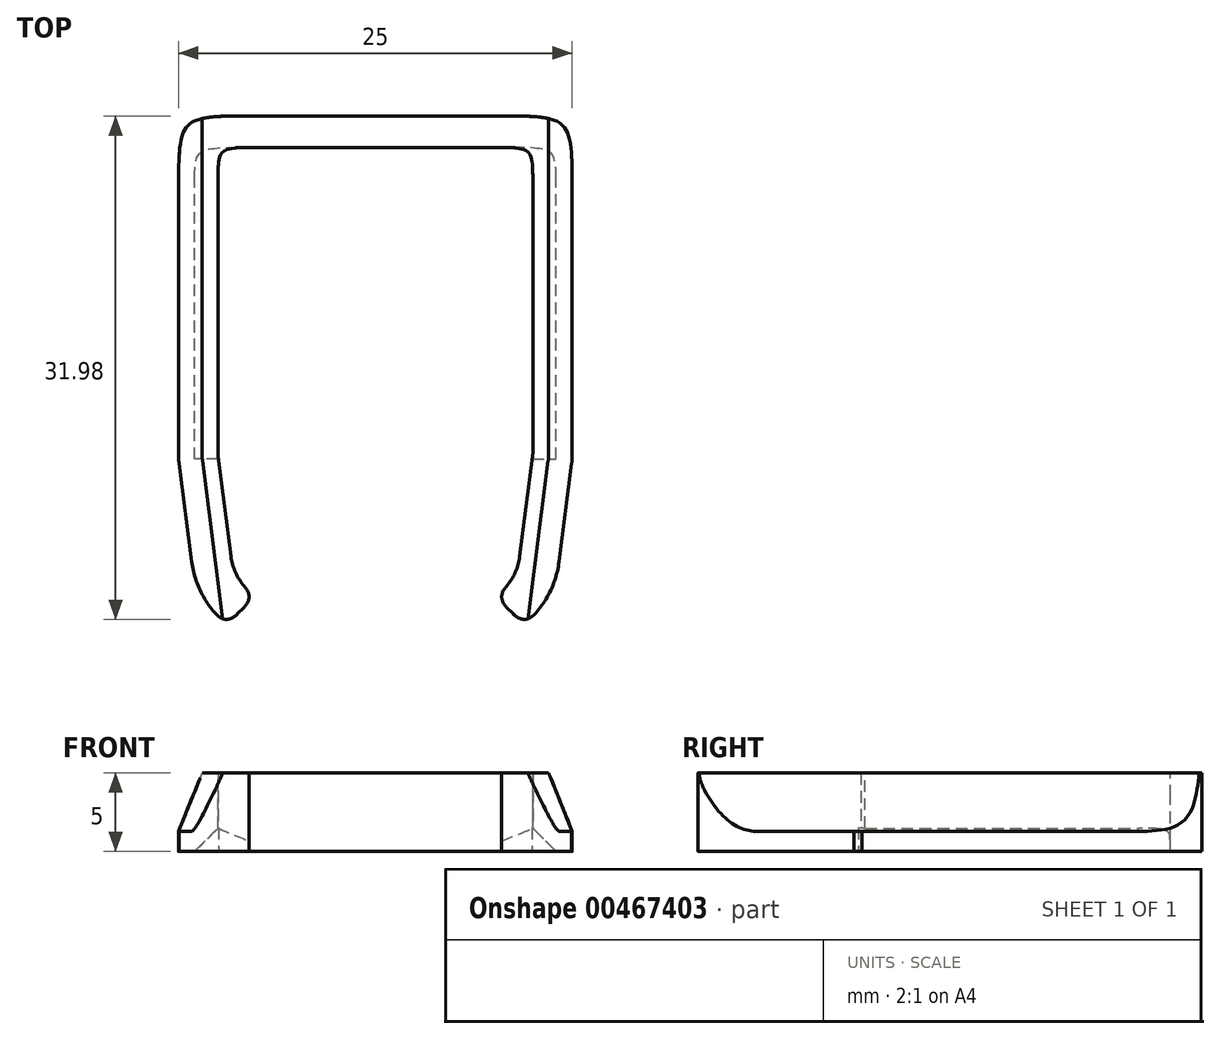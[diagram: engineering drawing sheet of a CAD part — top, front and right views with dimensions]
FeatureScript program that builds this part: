
annotation { "Feature Type Name" : "Feature", "Feature Type Description" : "" }
export const myFeature = defineFeature(function(context is Context, id is Id, definition is map)
    precondition{}
    {
        {
            var Q0;
            Q0=qCreatedBy(makeId("Top.planeOp"),FACE);
            var sketch = newSketch(context, id + "F0", { "sketchPlane" : qUnion([Q0])});
            skLineSegment(sketch, "E0", {"start": v(0, 0) * mm, "end": v(7.15, 0) * mm});
            skLineSegment(sketch, "E1", {"start": v(7.15, 0) * mm, "end": v(7.15, -3) * mm});
            skArc(sketch, "E2", {"start": v(8.15, -9.67) * mm, "mid": v(9.96, -5.99) * mm, "end": v(7.15, -3) * mm});
            skLineSegment(sketch, "E3", {"start": v(7.15, -3) * mm, "end": v(0, -3) * mm, "construction": true});
            skLineSegment(sketch, "E4", {"start": v(10, -6.52) * mm, "end": v(10, 0) * mm, "construction": true});
            skLineSegment(sketch, "E5", {"start": v(10, 0) * mm, "end": v(7.15, 0) * mm, "construction": true});
            skSolve(sketch);
        }
        {
            var Q0;
            Q0=qCreatedBy(makeId("Top.planeOp"),FACE);
            var sketch = newSketch(context, id + "F1", { "sketchPlane" : qUnion([Q0])});
            skLineSegment(sketch, "E6", {"start": v(0, 19) * mm, "end": v(0, 21) * mm});
            skLineSegment(sketch, "E7", {"start": v(0, 21) * mm, "end": v(12.5, 21) * mm});
            skLineSegment(sketch, "E8", {"start": v(9.42, -11.3) * mm, "end": v(7.62, -9.5) * mm});
            skLineSegment(sketch, "E9", {"start": v(0, 19) * mm, "end": v(10, 19) * mm});
            skLineSegment(sketch, "E10", {"start": v(10, -0.5) * mm, "end": v(9.17, -6.98) * mm});
            skArc(sketch, "E11", {"start": v(7.62, -9.5) * mm, "mid": v(8.67, -8.4) * mm, "end": v(9.17, -6.98) * mm});
            skLineSegment(sketch, "E12", {"start": v(12.5, -0.82) * mm, "end": v(11.67, -7.3) * mm});
            skArc(sketch, "E13", {"start": v(9.42, -11.3) * mm, "mid": v(10.94, -9.52) * mm, "end": v(11.67, -7.3) * mm});
            skLineSegment(sketch, "E14", {"start": v(12.5, 21) * mm, "end": v(12.5, -0.82) * mm});
            skLineSegment(sketch, "E15", {"start": v(10, 19) * mm, "end": v(10, -0.5) * mm});
            skLineSegment(sketch, "E16", {"start": v(10, 19) * mm, "end": v(12.5, 19) * mm, "construction": true});
            skLineSegment(sketch, "E17", {"start": v(10, -0.5) * mm, "end": v(12.5, -0.82) * mm, "construction": true});
            skSolve(sketch);
        }
        {
            var Q0;
            Q0=qSketchRegion(id+"F1",true);
            extrude(context, id + "F2", {"entities" : qUnion([Q0]), "depth" : 5 * mm});
        }
        {
            var Q0;
            Q0=makeQuery(id+"F2.opExtrude","SWEPT_EDGE",EDGE,{"disambiguationData":[OSD([sQuery(id+"F1.wireOp",EDGE,"E9"),sQuery(id+"F1.wireOp",EDGE,"E15")])]});
            var Q1;
            Q1=makeQuery(id+"F2.opExtrude","SWEPT_EDGE",EDGE,{"disambiguationData":[OSD([sQuery(id+"F1.wireOp",EDGE,"E10"),sQuery(id+"F1.wireOp",EDGE,"E15")])]});
            fillet(context, id + "F3", {"entities" : qUnion([Q0, Q1]), "radius" : 2 * mm, "tangentPropagation" : true, "rho" : .7, "crossSection" : FilletCrossSection.CONIC, "allowEdgeOverflow" : false});
        }
        {
            var Q0;
            Q0=makeQuery(id+"F2.opExtrude","SWEPT_EDGE",EDGE,{"disambiguationData":[OSD([sQuery(id+"F1.wireOp",EDGE,"E7"),sQuery(id+"F1.wireOp",EDGE,"E14")])]});
            var Q1;
            Q1=makeQuery(id+"F2.opExtrude","SWEPT_EDGE",EDGE,{"disambiguationData":[OSD([sQuery(id+"F1.wireOp",EDGE,"E12"),sQuery(id+"F1.wireOp",EDGE,"E14")])]});
            fillet(context, id + "F4", {"entities" : qUnion([Q0, Q1]), "radius" : 4 * mm, "tangentPropagation" : true, "rho" : .7, "crossSection" : FilletCrossSection.CONIC, "allowEdgeOverflow" : false});
        }
        {
            var Q0;
            Q0=makeQuery(id+"F2.opExtrude","SWEPT_FACE",FACE,{"disambiguationData":[OSD([sQuery(id+"F1.wireOp",EDGE,"E9")])]});
            var sketch = newSketch(context, id + "F5", { "sketchPlane" : qUnion([Q0])});
            skLineSegment(sketch, "E18.bottom", {"start": v(0, 2.5) * mm, "end": v(3, 2.5) * mm});
            skLineSegment(sketch, "E18.top", {"start": v(0, 0) * mm, "end": v(3, 0) * mm});
            skLineSegment(sketch, "E18.left", {"start": v(0, 2.5) * mm, "end": v(0, 0) * mm});
            skLineSegment(sketch, "E18.right", {"start": v(3, 2.5) * mm, "end": v(3, 0) * mm});
            skSolve(sketch);
        }
        {
            var Q0;
            Q0=makeQuery(id+"F13.opPattern","COPY",EDGE,{"derivedFrom":makeQuery(id+"F2.opExtrude","CAP_EDGE",EDGE,{"disambiguationData":[OSD([sQuery(id+"F1.wireOp",EDGE,"E12")])],"isStart":true}),"instanceName":"1"});
            var Q1;
            Q1=makeQuery(id+"F2.opExtrude","CAP_EDGE",EDGE,{"disambiguationData":[OSD([sQuery(id+"F1.wireOp",EDGE,"E12")])],"isStart":false});
            var Q2;
            Q2=makeQuery(id+"F2.opExtrude","CAP_EDGE",EDGE,{"disambiguationData":[OSD([sQuery(id+"F1.wireOp",EDGE,"E14")])],"isStart":false});
            chamfer(context, id + "F6", {"entities" : qUnion([Q0, Q1, Q2]), "chamferType" : ChamferType.OFFSET_ANGLE, "width" : 1.5 * mm, "oppositeDirection" : true, "angle" : 68 * degree});
        }
        {
            var Q0;
            {var subQ3=sQuery(id+"F5.wireOp",EDGE,"E18.bottom");Q0=makeQuery(id+"F5.imprint","IMPRINT",FACE,{"disambiguationData":[TD([[makeQuery(id+"F5.imprint","IMPRINT",EDGE,{"derivedFrom":subQ3}),1.0]])]});}
            var sketch = newSketch(context, id + "F7", { "sketchPlane" : qUnion([Q0])});
            skLineSegment(sketch, "E19", {"start": v(8, 3.48) * mm, "end": v(8, 0) * mm});
            skLineSegment(sketch, "E20", {"start": v(8, 0) * mm, "end": v(11.48, 0) * mm});
            skLineSegment(sketch, "E21", {"start": v(11.48, 0) * mm, "end": v(8, 3.48) * mm});
            skPoint(sketch, "E22", {"position": v(9.98, 0) * mm});
            skSolve(sketch);
        }
        {
            var Q0;
            Q0=qSketchRegion(id+"F7",true);
            extrude(context, id + "F8", {"entities" : qUnion([Q0]), "operationType" : NewBodyOperationType.REMOVE, "depth" : 19.8 * mm});
        }
        {
            var Q0;
            Q0=qCreatedBy(makeId("Front.planeOp"),FACE);
            cPlane(context, id + "F9", {"entities" : qUnion([Q0]), "cplaneType" : CPlaneType.OFFSET, "offset" : 0 * mm, "oppositeDirection" : true, "width" : 150 * mm, "height" : 150 * mm});
        }
        {
            var Q0;
            Q0=qCreatedBy(id+"F9.planeOp",FACE);
            var sketch = newSketch(context, id + "F10", { "sketchPlane" : qUnion([Q0])});
            skLineSegment(sketch, "E23", {"start": v(16.37, 0) * mm, "end": v(14.33, 5) * mm});
            skLineSegment(sketch, "E24", {"start": v(14.33, 5) * mm, "end": v(11.1, 5) * mm});
            skLineSegment(sketch, "E25", {"start": v(16.37, 0) * mm, "end": v(12.6, 0) * mm});
            skLineSegment(sketch, "E26", {"start": v(12.6, 0) * mm, "end": v(11.1, 5) * mm});
            skLineSegment(sketch, "E27", {"start": v(12.6, 1.29) * mm, "end": v(11.1, 5) * mm, "construction": true});
            skSolve(sketch);
        }
        {
            var Q0;
            Q0=makeQuery(id+"F2.opExtrude","SWEPT_EDGE",EDGE,{"disambiguationData":[OSD([sQuery(id+"F1.wireOp",EDGE,"E8"),sQuery(id+"F1.wireOp",EDGE,"E11")])]});
            var Q1;
            Q1=makeQuery(id+"F2.opExtrude","SWEPT_EDGE",EDGE,{"disambiguationData":[OSD([sQuery(id+"F1.wireOp",EDGE,"E8"),sQuery(id+"F1.wireOp",EDGE,"E13")])]});
            var Q2;
            Q2=makeQuery(id+"FeDOwkYFawgQy55_1.opExtrude","CAP_EDGE",EDGE,{"disambiguationData":[OSD([sQuery(id+"F10.wireOp",EDGE,"E23")])],"isStart":true});
            var Q3;
            Q3=makeQuery(id+"FeDOwkYFawgQy55_1.opExtrude","CAP_EDGE",EDGE,{"disambiguationData":[OSD([sQuery(id+"F10.wireOp",EDGE,"E23")])],"isStart":false});
            var Q4;
            Q4=makeQuery(id+"FeDOwkYFawgQy55_1.boolean.opBoolean","INTERSECT",EDGE,{"derivedFrom":[makeQuery(id+"F6.opChamfer","BLEND_FACE",FACE,{"disambiguationData":[OSD([sQuery(id+"F1.wireOp",EDGE,"E12")])]}),makeQuery(id+"FeDOwkYFawgQy55_1.opExtrude","CAP_FACE",FACE,{"disambiguationData":[OSD([sQuery(id+"F10.wireOp",EDGE,"E23"),sQuery(id+"F10.wireOp",EDGE,"E24"),sQuery(id+"F10.wireOp",EDGE,"E25"),sQuery(id+"F10.wireOp",EDGE,"E26")])],"isStart":true})]});
            var Q5;
            Q5=makeQuery(id+"FeDOwkYFawgQy55_1.boolean.opBoolean","INTERSECT",EDGE,{"derivedFrom":[makeQuery(id+"F6.opChamfer","BLEND_FACE",FACE,{"disambiguationData":[OSD([sQuery(id+"F1.wireOp",EDGE,"E12")])]}),makeQuery(id+"FeDOwkYFawgQy55_1.opExtrude","CAP_FACE",FACE,{"disambiguationData":[OSD([sQuery(id+"F10.wireOp",EDGE,"E23"),sQuery(id+"F10.wireOp",EDGE,"E24"),sQuery(id+"F10.wireOp",EDGE,"E25"),sQuery(id+"F10.wireOp",EDGE,"E26")])],"isStart":false})]});
            var Q6;
            Q6=makeQuery(id+"FeDOwkYFawgQy55_1.boolean.opBoolean","INTERSECT",EDGE,{"derivedFrom":[makeQuery(id+"F2.opExtrude","SWEPT_FACE",FACE,{"disambiguationData":[OSD([sQuery(id+"F1.wireOp",EDGE,"E12")])]}),makeQuery(id+"FeDOwkYFawgQy55_1.opExtrude","CAP_FACE",FACE,{"disambiguationData":[OSD([sQuery(id+"F10.wireOp",EDGE,"E23"),sQuery(id+"F10.wireOp",EDGE,"E24"),sQuery(id+"F10.wireOp",EDGE,"E25"),sQuery(id+"F10.wireOp",EDGE,"E26")])],"isStart":false})]});
            var Q7;
            Q7=makeQuery(id+"FeDOwkYFawgQy55_1.boolean.opBoolean","INTERSECT",EDGE,{"derivedFrom":[makeQuery(id+"F2.opExtrude","SWEPT_FACE",FACE,{"disambiguationData":[OSD([sQuery(id+"F1.wireOp",EDGE,"E12")])]}),makeQuery(id+"FeDOwkYFawgQy55_1.opExtrude","CAP_FACE",FACE,{"disambiguationData":[OSD([sQuery(id+"F10.wireOp",EDGE,"E23"),sQuery(id+"F10.wireOp",EDGE,"E24"),sQuery(id+"F10.wireOp",EDGE,"E25"),sQuery(id+"F10.wireOp",EDGE,"E26")])],"isStart":true})]});
            fillet(context, id + "F11", {"entities" : qUnion([Q0, Q1, Q2, Q3, Q4, Q5, Q6, Q7]), "radius" : 1 * mm, "tangentPropagation" : true, "rho" : .5, "crossSection" : FilletCrossSection.CONIC, "allowEdgeOverflow" : false});
        }
        {
            var Q0;
            Q0=makeQuery(id+"F8.boolean.opBoolean","COPY",EDGE,{"derivedFrom":makeQuery(id+"F8.opExtrude","CAP_EDGE",EDGE,{"disambiguationData":[OSD([sQuery(id+"F7.wireOp",EDGE,"E21")])],"isStart":true})});
            fillet(context, id + "F12", {"entities" : qUnion([Q0]), "radius" : 2 * mm, "tangentPropagation" : true, "rho" : .7, "crossSection" : FilletCrossSection.CONIC, "allowEdgeOverflow" : false});
        }
        {
            var Q0;
            Q0=makeQuery(id+"F2.opExtrude","SWEPT_BODY",BODY,{"disambiguationData":[OSD([sQuery(id+"F1.wireOp",EDGE,"E6"),sQuery(id+"F1.wireOp",EDGE,"E7"),sQuery(id+"F1.wireOp",EDGE,"E8"),sQuery(id+"F1.wireOp",EDGE,"E9"),sQuery(id+"F1.wireOp",EDGE,"E10"),sQuery(id+"F1.wireOp",EDGE,"E11"),sQuery(id+"F1.wireOp",EDGE,"E12"),sQuery(id+"F1.wireOp",EDGE,"E13")])]});
            var Q1;
            Q1=makeQuery(id+"FEYfMAQslLhMSq6_1.boolean.opBoolean","MERGE",FACE,{"derivedFrom":[makeQuery(id+"F2.opExtrude","SWEPT_FACE",FACE,{"disambiguationData":[OSD([sQuery(id+"F1.wireOp",EDGE,"E6")])]}),makeQuery(id+"FEYfMAQslLhMSq6_1.opExtrude","SWEPT_FACE",FACE,{"disambiguationData":[OSD([sQuery(id+"F5.wireOp",EDGE,"E18.left")])]})]});
            mirror(context, id + "F13", {"operationType" : NewBodyOperationType.ADD, "entities" : qUnion([Q0]), "mirrorPlane" : qUnion([Q1])});
        }
    });
